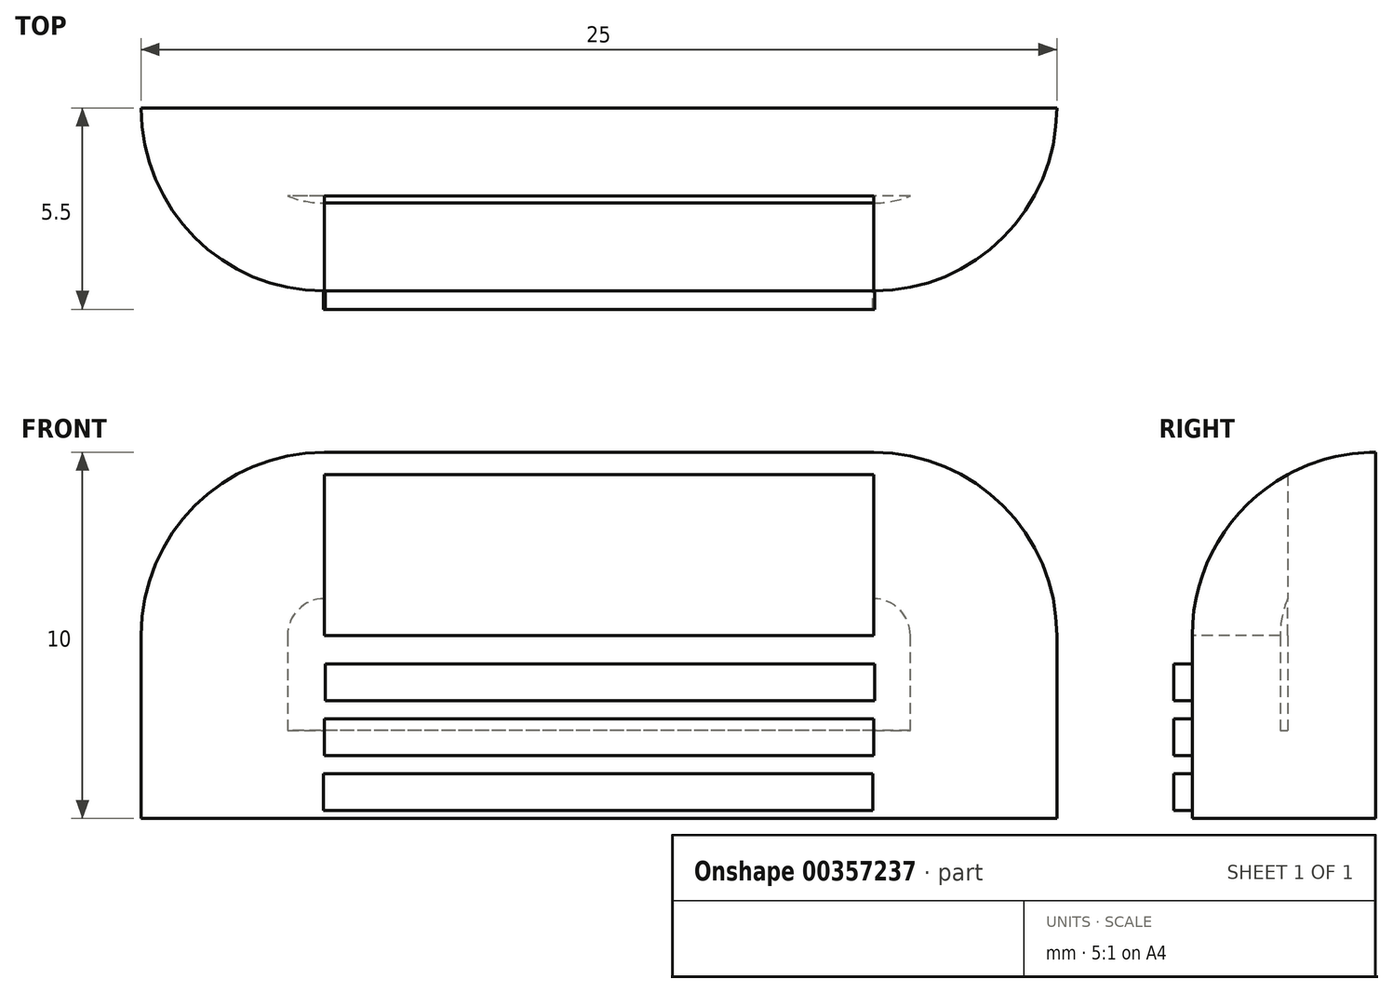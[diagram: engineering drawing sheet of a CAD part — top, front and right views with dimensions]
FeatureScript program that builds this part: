
annotation { "Feature Type Name" : "Feature", "Feature Type Description" : "" }
export const myFeature = defineFeature(function(context is Context, id is Id, definition is map)
    precondition{}
    {
        {
            var Q0;
            Q0=qCreatedBy(makeId("Top.planeOp"),FACE);
            var sketch = newSketch(context, id + "F0", { "sketchPlane" : qUnion([Q0])});
            skLineSegment(sketch, "E0.bottom", {"start": v(12.5, -2.5) * mm, "end": v(-12.5, -2.5) * mm});
            skLineSegment(sketch, "E0.top", {"start": v(12.5, 2.5) * mm, "end": v(-12.5, 2.5) * mm});
            skLineSegment(sketch, "E0.left", {"start": v(12.5, -2.5) * mm, "end": v(12.5, 2.5) * mm});
            skLineSegment(sketch, "E0.right", {"start": v(-12.5, -2.5) * mm, "end": v(-12.5, 2.5) * mm});
            skPoint(sketch, "E0.middle", {"position": v(0, 0) * mm});
            skSolve(sketch);
        }
        {
            var Q0;
            Q0 = qSketchRegion(id + "F0", true);
            extrude(context, id + "F1", {"entities" : qUnion([Q0]), "depth" : 10 * mm});
        }
        {
            var Q0;
            Q0=makeQuery(id+"F1.opExtrude","CAP_EDGE",EDGE,{"disambiguationData":[OSD([sQuery(id+"F0.wireOp",EDGE,"E0.bottom")])],"isStart":false});
            fillet(context, id + "F2", {"entities" : qUnion([Q0]), "radius" : 5 * mm, "tangentPropagation" : true, "allowEdgeOverflow" : false});
        }
        {
            var Q0;
            Q0=makeQuery(id+"F2.opFillet","BLEND_EDGE",EDGE,{"blendedFrom":[makeQuery(id+"F1.opExtrude","CAP_EDGE",EDGE,{"disambiguationData":[OSD([sQuery(id+"F0.wireOp",EDGE,"E0.bottom")])],"isStart":false}),makeQuery(id+"F1.opExtrude","SWEPT_FACE",FACE,{"disambiguationData":[OSD([sQuery(id+"F0.wireOp",EDGE,"E0.left")])]})],"blendedInto":[makeQuery(id+"F1.opExtrude","SWEPT_FACE",FACE,{"disambiguationData":[OSD([sQuery(id+"F0.wireOp",EDGE,"E0.left")])]})]});
            var Q1;
            Q1=makeQuery(id+"F2.opFillet","BLEND_EDGE",EDGE,{"blendedFrom":[makeQuery(id+"F1.opExtrude","CAP_EDGE",EDGE,{"disambiguationData":[OSD([sQuery(id+"F0.wireOp",EDGE,"E0.bottom")])],"isStart":false}),makeQuery(id+"F1.opExtrude","SWEPT_FACE",FACE,{"disambiguationData":[OSD([sQuery(id+"F0.wireOp",EDGE,"E0.right")])]})],"blendedInto":[makeQuery(id+"F1.opExtrude","SWEPT_FACE",FACE,{"disambiguationData":[OSD([sQuery(id+"F0.wireOp",EDGE,"E0.right")])]})]});
            fillet(context, id + "F3", {"entities" : qUnion([Q0, Q1]), "radius" : 5 * mm, "tangentPropagation" : true, "allowEdgeOverflow" : false});
        }
        {
            var Q0;
            Q0=qCreatedBy(makeId("Front.planeOp"),FACE);
            var sketch = newSketch(context, id + "F4", { "sketchPlane" : qUnion([Q0])});
            skLineSegment(sketch, "E1", {"start": v(-7.47, 4.22) * mm, "end": v(7.53, 4.22) * mm});
            skLineSegment(sketch, "E2", {"start": v(7.53, 4.22) * mm, "end": v(7.53, 3.22) * mm});
            skLineSegment(sketch, "E3", {"start": v(7.53, 3.22) * mm, "end": v(-7.47, 3.22) * mm});
            skLineSegment(sketch, "E4", {"start": v(-7.47, 3.22) * mm, "end": v(-7.47, 4.22) * mm});
            skLineSegment(sketch, "E5.1.0.0", {"start": v(7.5, 1.72) * mm, "end": v(-7.5, 1.72) * mm});
            skLineSegment(sketch, "E5.1.0.1", {"start": v(-7.5, 2.72) * mm, "end": v(7.5, 2.72) * mm});
            skLineSegment(sketch, "E5.1.0.2", {"start": v(-7.5, 1.72) * mm, "end": v(-7.5, 2.72) * mm});
            skLineSegment(sketch, "E5.1.0.3", {"start": v(7.5, 2.72) * mm, "end": v(7.5, 1.72) * mm});
            skLineSegment(sketch, "E5.2.0.0", {"start": v(7.47, 0.22) * mm, "end": v(-7.53, 0.22) * mm});
            skLineSegment(sketch, "E5.2.0.1", {"start": v(-7.53, 1.22) * mm, "end": v(7.47, 1.22) * mm});
            skLineSegment(sketch, "E5.2.0.2", {"start": v(-7.53, 0.22) * mm, "end": v(-7.53, 1.22) * mm});
            skLineSegment(sketch, "E5.2.0.3", {"start": v(7.47, 1.22) * mm, "end": v(7.47, 0.22) * mm});
            skLineSegment(sketch, "E5.direction1", {"start": v(-7.47, 3.22) * mm, "end": v(-7.5, 1.72) * mm, "construction": true});
            skSolve(sketch);
        }
        {
            var Q0;
            Q0 = qSketchRegion(id + "F4", true);
            extrude(context, id + "F5", {"entities" : qUnion([Q0]), "operationType" : NewBodyOperationType.ADD, "depth" : 3 * mm});
        }
        {
            var Q0;
            Q0=makeQuery(id+"F2.opFillet","BLEND_FACE",FACE,{"disambiguationData":[OSD([sQuery(id+"F0.wireOp",EDGE,"E0.bottom")])]});
            shell(context, id + "F6", {"entities" : qUnion([Q0]), "thickness" : 2.4 * mm});
        }
    });
